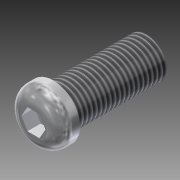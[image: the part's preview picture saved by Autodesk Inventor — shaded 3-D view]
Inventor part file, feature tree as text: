
AUTODESK INVENTOR PART (.ipt)
format: ipt  version: 2015 (Build 190159000, 159)  size: 124,928 bytes
history: native  units: mm
features: extrude x3, sketch x3, fillet x1, thread x1
ambient origin geometry x8: Origin, YZ Plane, XZ Plane, XY Plane, X Axis, Y Axis, Z Axis, Center Point
bodies: Solid1 (feature_tree)
feature tree (8):
  extrude  "Extrusion1"  Depth=1.5mm TaperAngle=0.0deg
  extrude  "Extrusion2"  Depth=7.0mm TaperAngle=0.0deg
  extrude  "Extrusion3"  Depth=1.0mm
  fillet  "Fillet1"  Radius=10.0mm
  thread  "Thread1"  [1 undecoded]
  sketch  "Sketch1"  dims[d0=4.0mm d1=1.5mm d2=0.0mm]
  sketch  "Sketch2"  dims[d3=3.0mm d4=7.0mm d5=0.0mm]
  sketch  "Sketch3"  dims[d6=1.0mm d7=0.0mm d8=1.0mm d9=10.0mm d10=0.0mm]
note: 1 required parameter value undecoded (feature->parameter linkage not recoverable at this tier; creation-order binding heuristic only, values carry confidence <= 0.55)
